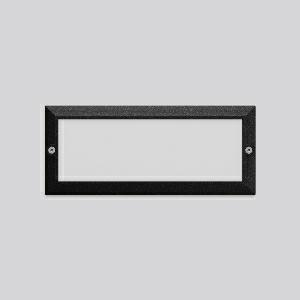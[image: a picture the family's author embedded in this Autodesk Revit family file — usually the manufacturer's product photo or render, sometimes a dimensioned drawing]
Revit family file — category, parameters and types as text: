
# Revit family: brick_steps_641306_0031_1_76_b546
name_source: partatom
category: Lighting Fixtures
units: mm (PartAtom-declared; Revit-internal decimal feet)

## family parameters
Cut with Voids When Loaded = No
Host = Face
Light Source = No
Part Type = Normal
Room Calculation Point = No
Round Connector Dimension = Use Diameter
Shared = No

## types (1)
- BRICK STEPS (1 x LED Modul 840, 200 lm, 4000)
    Apparent Load = 6 VA
    CIE Flux Codes = 12 36 66 50 100
    Color Rendering = 80
    Color Temperature = 4000
    Default Elevation = 1800 mm
    Description = Series: BRICK STEPS
Robust LED wall and step luminaires. Housing and cover frame: die-cast aluminium, powder-coated. Shock resistant plastic (polycarbonate) cover, opal. Driver integrated. With second cable entry for loop through. Recommended accessory: recessed support. 
Colour: anthracite metallic (DB703)
Length: 236 mm
Width: 100 mm
Height: 5 mm
Lamp: LED
System power: 6 W
Rated luminous flux: 200 lm
Luminous efficiency: 33 lm/W
Control gear: Converter, dimmable, DALI
Protection class: I
Type of protection: IP 66
    Height = 5 mm  [stored 0.0164042 ft]
    Lamp = 1 x LED Modul 840
    Lamp Light Flux = 200 lm
    Lamp count = 1
    Length = 236 mm
    Lifetime = 50000 h
    Luminous efficacy = 33 lm/W
    Manufacturer = RZB
    ModVariant = No
    Model = 641306.0031.1.76
    Mounting Place = Wall
    Mounting Type = Recessed
    Number of Poles = 1
    OnlyDefault = Yes
    Power Factor = 1
    Product Name = BRICK STEPS
    Product group = Recessed wall luminaires
    ProductGroupID = 2004
    Protection Class = Protection class I
    Protection Degree = IP 66
    RLX_Detail_Level = 1
    RLX_Emergency_Light_Flux = 0 lm
    RLX_Emergency_Type = 0
    RLX_Emergency_Type_DB = No
    RlxData = <blob elided: 35141 chars, md5=511771d9>
    Socket = socket
    Standby Power = 0 W
    System Light Flux = 200 lm
    System Power = 6 W
    Type Comments = Product without accessories
    Type Image = 641306.0031.jpg
    URL = http://relux.com
    VarID = ---
    Voltage = 230 V
    Voltage Range = 220-240 V
    Weight = 0.00 kg
    Width = 100 mm  [stored 0.328084 ft]

note: [stored X ft] marks values corroborated as IEEE doubles in the binary element streams (Revit-internal decimal feet)

## geometry (parser evidence)
native form markers: Blend x4, Sweep x12
no freeform markers — native parametric forms only
